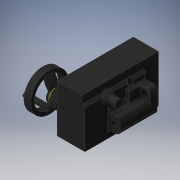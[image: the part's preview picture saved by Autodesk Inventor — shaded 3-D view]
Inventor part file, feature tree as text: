
AUTODESK INVENTOR PART (.ipt)
format: ipt  version: 2016 (Build 200138000, 138)  size: 587,264 bytes
history: native  units: in
note: dims shown in document units (in); Inventor stores cm internally (conversion verified against a paired STEP export)
features: sketch x20, extrude x16, fillet x6, plane x3, loft x2, projected_geometry x2, chamfer x1, other x1
ambient origin geometry x8: Origin, YZ Plane, XZ Plane, XY Plane, X Axis, Y Axis, Z Axis, Center Point
bodies: Solid1 (feature_tree)
feature tree (51):
  extrude  "Extrusion1"  Depth=4.3701in
  extrude  "Extrusion2"  Depth=1.1811in
  extrude  "Extrusion3"  Depth=12.0079in TaperAngle=0.0deg
  extrude  "Extrusion4"  Depth=12.0079in TaperAngle=0.0deg
  extrude  "Extrusion5"  Depth=1.9685in
  extrude  "Extrusion6"  Depth=1.4567in TaperAngle=0.0deg
  extrude  "Extrusion7"  Depth=4.6457in TaperAngle=0.0deg
  fillet  "Fillet2"  Radius=1.7717in
  chamfer  "Chamfer1"  Distance=0.5512in
  fillet  "Fillet3"  Radius=0.7874in
  extrude  "Extrusion8"  Depth=0.5118in TaperAngle=0.0deg
  extrude  "Extrusion9"  Depth=0.315in
  extrude  "Extrusion10"  Depth=0.2559in TaperAngle=0.0deg
  fillet  "Fillet4"  Radius=0.5906in
  extrude  "Extrusion11"  Depth=0.0787in
  extrude  "Extrusion12"  Depth=0.0787in
  sketch  "Sketch14"  dims[d39=0.9449in d40=0.7874in]
  plane  "Work Plane2"
  loft  "Loft1"
  plane  "Work Plane3"
  extrude  "Extrusion13"  Depth=1.1417in
  extrude  "Extrusion15"  Depth=1.7717in
  plane  "Work Plane5"
  sketch  "Sketch22"  dims[d55=3.3071in d56=1.1811in]
  sketch  "Sketch16"  dims[d43=0.2559in d44=0.0in d45=1.7717in]
  loft  "Loft2"
  fillet  "Fillet5"  Radius=0.8268in
  extrude  "Extrusion16"  Depth=1.4173in TaperAngle=0.0deg
  fillet  "Fillet6"  Radius=0.1181in
  fillet  "Fillet7"  Radius=2.7559in
  extrude  "Extrusion17"  Depth=1.1811in
  sketch  "Sketch1"  dims[d0=3.937in d1=4.3701in]
  sketch  "Sketch2"  dims[d2=7.4803in d3=1.1811in]
  sketch  "Sketch3"  dims[d4=5.9843in d5=12.0079in d6=0.0in]
  sketch  "Sketch4"  dims[d7=2.3228in d8=12.0079in d9=0.0in]
  sketch  "Sketch5"  dims[d10=0.7087in d11=1.9685in]
  sketch  "Sketch6"  dims[d12=3.8976in d13=1.4567in d14=0.0in]
  sketch  "Sketch7"  dims[d15=1.5748in d16=4.6457in d17=0.0in d18=1.7717in d19=0.5512in d20=0.0in d21=0.7874in]
  sketch  "Sketch9"  dims[d22=0.7874in d23=0.5118in d24=0.0in]
  sketch  "Sketch10"  dims[d25=2.3622in d26=0.315in]
  sketch  "Sketch11"  dims[d27=0.5906in d28=0.2559in d29=0.0in d31=0.5906in]
  sketch  "Sketch12"  dims[d32=0.5118in d33=0.0787in d34=45.0deg d36=1.1811in]
  sketch  "Sketch13"  dims[d37=1.6142in d38=0.0787in]
  projected_geometry  "Projected Loop1"
  sketch  "Sketch15"  dims[d41=0.9646in d42=1.1417in]
  other  "Edges1"
  sketch  "Sketch18"  dims[d46=1.5748in d47=3.5827in d48=0.8268in d49=0.0in]
  sketch  "Sketch21"  dims[d50=1.2205in d51=1.4173in d52=0.0in d53=0.1181in d54=2.7559in]
  projected_geometry  "Projected Loop4"
  sketch  "Sketch23"  dims[d57=1.1417in d58=0.0in]
  sketch  "Sketch24"  dims[d59=2.2047in d60=0.2756in d61=0.0in d62=0.9449in d63=5.1181in d64=0.0in d65=90.0deg d66=0.0in d67=90.0deg d68=0.6693in d69=2.2047in d71=0.0in d72=90.0deg d75=2.2047in d76=4.7244in d78=0.7874in d79=0.5118in d80=0.2756in d81=0.0in d82=2.7559in d87=5.9843in d88=4.8031in d89=1.063in d90=0.0in d91=1.7717in d92=0.0in d93=90.0deg d94=0.5906in d95=0.7874in d96=2.2047in d97=1.063in d98=0.0in d99=0.0787in d100=0.0787in d101=2.7559in d102=0.0in]
